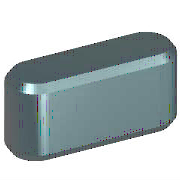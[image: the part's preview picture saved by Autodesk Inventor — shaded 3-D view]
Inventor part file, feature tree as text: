
AUTODESK INVENTOR PART (.ipt)
format: ipt  version: 2015 (Build 190159000, 159)  size: 136,192 bytes
history: native  units: mm (DEFAULTED — no unit token found)
features: plane x3, extrude x1
ambient origin geometry x8: Origin, YZ Plane, XZ Plane, XY Plane, X Axis, Y Axis, Z Axis, Center Point
bodies: Solid1 (feature_tree)
feature tree (4):
  plane  "Work Plane1"
  plane  "Work Plane2"
  extrude  "轴承体1"  Depth=3.0mm
  plane  "Work Plane3"
